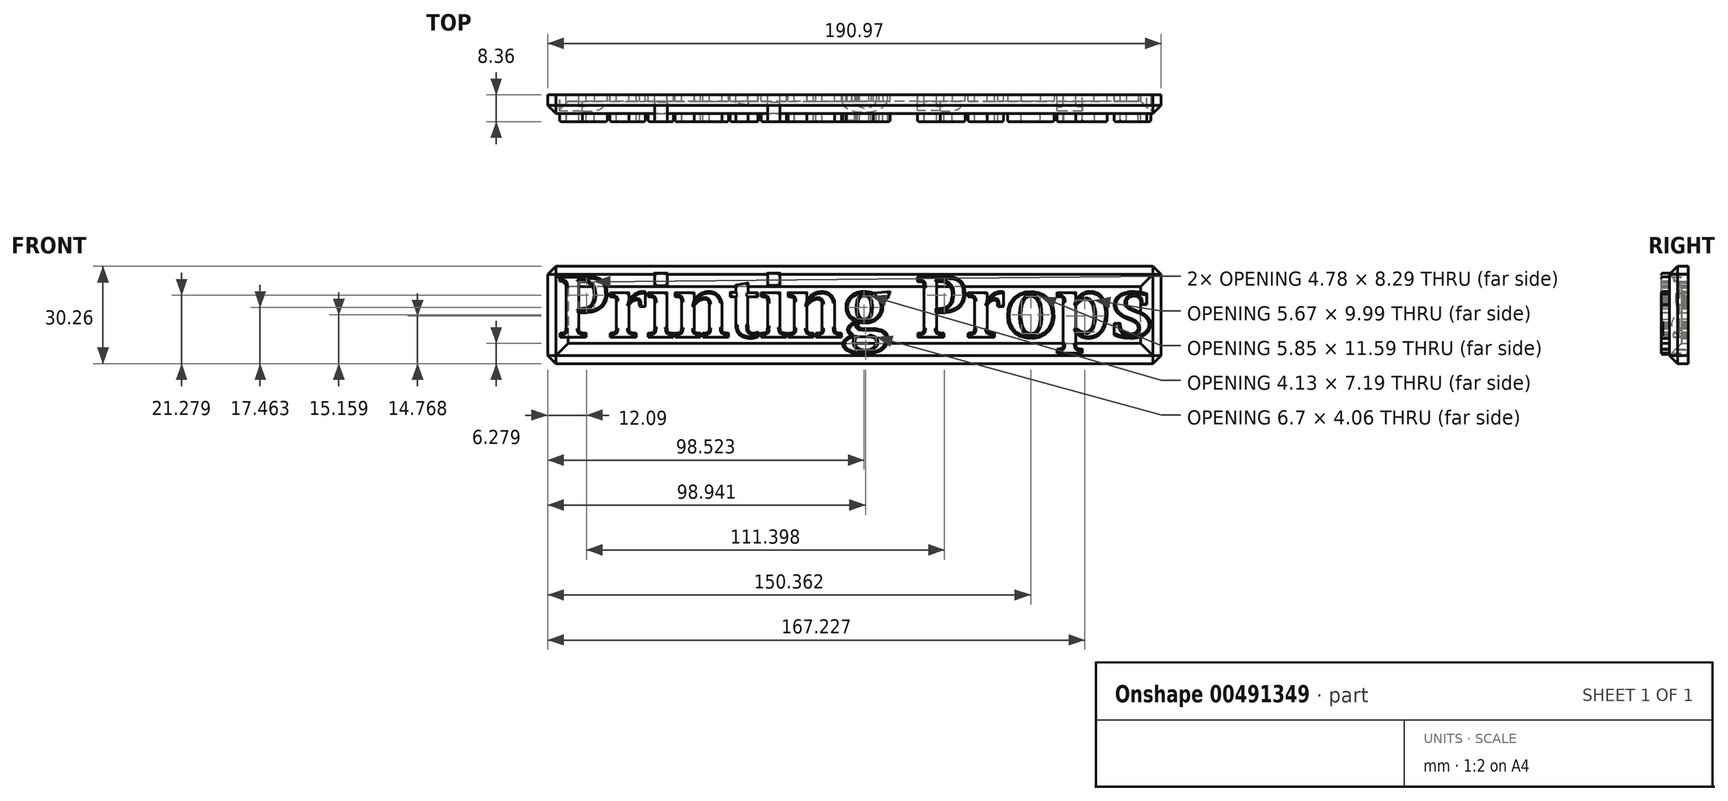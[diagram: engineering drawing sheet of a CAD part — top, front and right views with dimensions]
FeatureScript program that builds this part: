
annotation { "Feature Type Name" : "Feature", "Feature Type Description" : "" }
export const myFeature = defineFeature(function(context is Context, id is Id, definition is map)
    precondition{}
    {
        {
            var Q0;
            Q0=qCreatedBy(makeId("Front.planeOp"),FACE);
            var sketch = newSketch(context, id + "F0", { "sketchPlane" : qUnion([Q0])});
            skFitSpline(sketch, "E0", {"points": [v(-91.94, 12.22) * mm, v(-90.8, 12.2) * mm, v(-90.49, 12.06) * mm, v(-90.18, 11.82) * mm, v(-89.99, 10.88) * mm, v(-89.99, 10.32) * mm], "startDerivative": vector(4.95, 0.12) * mm, "endDerivative": vector(-0.1, -2.65) * mm});
            skFitSpline(sketch, "E1", {"points": [v(-91.84, -3.83) * mm, v(-90.83, -3.75) * mm, v(-90.33, -3.57) * mm, v(-90.09, -3.28) * mm, v(-89.99, -2.24) * mm], "startDerivative": vector(3.66, 0.14) * mm, "endDerivative": vector(0.08, 3.99) * mm});
            skFitSpline(sketch, "E2", {"points": [v(-85.99, -2.4) * mm, v(-85.92, -3.1) * mm, v(-85.68, -3.5) * mm, v(-85.3, -3.66) * mm, v(-84.73, -3.78) * mm, v(-83.76, -3.84) * mm], "startDerivative": vector(0.24, -3.52) * mm, "endDerivative": vector(4.1, -0.16) * mm});
            skFitSpline(sketch, "E3", {"points": [v(-85.98, 3.82) * mm, v(-84.6, 3.86) * mm, v(-83.12, 4.26) * mm, v(-82, 5.23) * mm, v(-81.55, 6.04) * mm, v(-81.33, 6.77) * mm, v(-81.2, 7.96) * mm, v(-81.24, 9.19) * mm, v(-81.58, 10.46) * mm, v(-82.35, 11.4) * mm, v(-83.21, 11.9) * mm, v(-83.91, 12.1) * mm, v(-85.98, 12.12) * mm], "startDerivative": vector(15.1, -0.2) * mm, "endDerivative": vector(-22.29, -0.17) * mm});
            skLineSegment(sketch, "E4", {"start": v(-85.98, 3.82) * mm, "end": v(-85.98, 12.12) * mm});
            skLineSegment(sketch, "E5", {"start": v(-89.99, 10.32) * mm, "end": v(-89.99, -2.24) * mm});
            skLineSegment(sketch, "E6", {"start": v(-85.99, -2.4) * mm, "end": v(-85.99, 2.51) * mm});
            skLineSegment(sketch, "E7", {"start": v(-91.94, 12.22) * mm, "end": v(-91.94, 13.6) * mm});
            skLineSegment(sketch, "E8", {"start": v(-91.94, 13.6) * mm, "end": v(-84.84, 13.6) * mm});
            skLineSegment(sketch, "E9", {"start": v(-91.84, -3.83) * mm, "end": v(-91.84, -5.1) * mm});
            skLineSegment(sketch, "E10", {"start": v(-91.84, -5.1) * mm, "end": v(-83.75, -5.1) * mm});
            skLineSegment(sketch, "E11", {"start": v(-83.75, -5.1) * mm, "end": v(-83.76, -3.84) * mm});
            skFitSpline(sketch, "E12", {"points": [v(-85.99, 2.51) * mm, v(-84.25, 2.51) * mm, v(-82.64, 2.64) * mm, v(-81.06, 2.99) * mm, v(-79.6, 3.66) * mm, v(-78.84, 4.24) * mm, v(-78.27, 4.85) * mm, v(-77.7, 5.78) * mm, v(-77.36, 6.72) * mm, v(-77.18, 7.66) * mm, v(-77.17, 8.86) * mm, v(-77.28, 10.04) * mm, v(-77.43, 10.75) * mm, v(-77.95, 11.78) * mm, v(-79.12, 12.92) * mm, v(-80.63, 13.48) * mm, v(-82.62, 13.65) * mm, v(-84.84, 13.6) * mm], "startDerivative": vector(26.06, -0.41) * mm, "endDerivative": vector(-29.4, -1.03) * mm});
            skLineSegment(sketch, "E13", {"start": v(-76.28, 7.51) * mm, "end": v(-76.28, 8.8) * mm});
            skLineSegment(sketch, "E14", {"start": v(-76.28, 8.8) * mm, "end": v(-70.38, 8.8) * mm});
            skLineSegment(sketch, "E15", {"start": v(-70.38, 8.8) * mm, "end": v(-70.38, 6.34) * mm});
            skLineSegment(sketch, "E16", {"start": v(-67.05, 4.44) * mm, "end": v(-65.31, 4.44) * mm});
            skLineSegment(sketch, "E17", {"start": v(-65.31, 4.44) * mm, "end": v(-65.31, 9.03) * mm});
            skLineSegment(sketch, "E18", {"start": v(-74.3, -2.36) * mm, "end": v(-74.3, 6.22) * mm});
            skLineSegment(sketch, "E19", {"start": v(-70.4, 4.83) * mm, "end": v(-70.4, -2.36) * mm});
            skLineSegment(sketch, "E20", {"start": v(-76.24, -3.81) * mm, "end": v(-76.24, -5.12) * mm});
            skLineSegment(sketch, "E21", {"start": v(-76.24, -5.12) * mm, "end": v(-68.07, -5.12) * mm});
            skLineSegment(sketch, "E22", {"start": v(-68.07, -5.12) * mm, "end": v(-68.07, -3.81) * mm});
            skFitSpline(sketch, "E23", {"points": [v(-76.28, 7.51) * mm, v(-75.6, 7.46) * mm, v(-75.08, 7.36) * mm, v(-74.68, 7.2) * mm, v(-74.47, 7) * mm, v(-74.35, 6.6) * mm, v(-74.3, 6.22) * mm], "startDerivative": vector(3.37, -0.21) * mm, "endDerivative": vector(0.24, -2.36) * mm});
            skFitSpline(sketch, "E24", {"points": [v(-70.38, 6.34) * mm, v(-69.87, 7.08) * mm, v(-69.4, 7.6) * mm, v(-68.86, 8.07) * mm, v(-68.26, 8.49) * mm, v(-67.53, 8.82) * mm, v(-66.76, 9.03) * mm, v(-65.99, 9.09) * mm, v(-65.31, 9.03) * mm], "startDerivative": vector(3.79, 5.74) * mm, "endDerivative": vector(5.61, -0.62) * mm});
            skFitSpline(sketch, "E25", {"points": [v(-70.4, 4.83) * mm, v(-70.07, 5.24) * mm, v(-69.6, 5.77) * mm, v(-69.03, 6.16) * mm, v(-68.41, 6.4) * mm, v(-67.8, 6.46) * mm, v(-67.47, 6.4) * mm, v(-67.3, 6.17) * mm, v(-67.05, 4.44) * mm], "startDerivative": vector(2.76, 3.54) * mm, "endDerivative": vector(1, -10.28) * mm});
            skFitSpline(sketch, "E26", {"points": [v(-76.24, -3.81) * mm, v(-75.25, -3.73) * mm, v(-74.8, -3.6) * mm, v(-74.51, -3.42) * mm, v(-74.37, -3.01) * mm, v(-74.3, -2.36) * mm], "startDerivative": vector(4.1, 0.22) * mm, "endDerivative": vector(0.3, 3.1) * mm});
            skFitSpline(sketch, "E27", {"points": [v(-70.4, -2.36) * mm, v(-70.27, -3.13) * mm, v(-70.04, -3.49) * mm, v(-69.6, -3.65) * mm, v(-68.92, -3.78) * mm, v(-68.07, -3.81) * mm], "startDerivative": vector(0.38, -3.73) * mm, "endDerivative": vector(3.76, -0.02) * mm});
            skLineSegment(sketch, "E28.bottom", {"start": v(-62.4, 14.84) * mm, "end": v(-58.48, 14.84) * mm});
            skLineSegment(sketch, "E28.top", {"start": v(-62.4, 10.95) * mm, "end": v(-58.48, 10.95) * mm});
            skLineSegment(sketch, "E28.left", {"start": v(-62.4, 14.84) * mm, "end": v(-62.4, 10.95) * mm});
            skLineSegment(sketch, "E28.right", {"start": v(-58.48, 14.84) * mm, "end": v(-58.48, 10.95) * mm});
            skLineSegment(sketch, "E29", {"start": v(-64.35, 7.53) * mm, "end": v(-64.35, 8.77) * mm});
            skLineSegment(sketch, "E30", {"start": v(-64.35, 8.77) * mm, "end": v(-58.52, 8.77) * mm});
            skLineSegment(sketch, "E31", {"start": v(-58.52, 8.77) * mm, "end": v(-58.52, -2.05) * mm});
            skLineSegment(sketch, "E32", {"start": v(-56.5, -3.83) * mm, "end": v(-56.5, -5.1) * mm});
            skLineSegment(sketch, "E33", {"start": v(-56.5, -5.1) * mm, "end": v(-64.37, -5.1) * mm});
            skLineSegment(sketch, "E34", {"start": v(-64.37, -5.1) * mm, "end": v(-64.37, -3.83) * mm});
            skLineSegment(sketch, "E35", {"start": v(-62.38, 5.71) * mm, "end": v(-62.38, -1.9) * mm});
            skFitSpline(sketch, "E36", {"points": [v(-64.35, 7.53) * mm, v(-63.53, 7.44) * mm, v(-62.95, 7.29) * mm, v(-62.64, 7.06) * mm, v(-62.47, 6.74) * mm, v(-62.4, 6.24) * mm, v(-62.38, 5.71) * mm], "startDerivative": vector(4.02, -0.33) * mm, "endDerivative": vector(0.08, -3.14) * mm});
            skFitSpline(sketch, "E37", {"points": [v(-64.37, -3.83) * mm, v(-63.3, -3.75) * mm, v(-62.9, -3.62) * mm, v(-62.65, -3.46) * mm, v(-62.5, -3.1) * mm, v(-62.38, -1.9) * mm], "startDerivative": vector(4.6, 0.22) * mm, "endDerivative": vector(0.28, 4.9) * mm});
            skFitSpline(sketch, "E38", {"points": [v(-58.52, -2.05) * mm, v(-58.43, -3.02) * mm, v(-58.18, -3.57) * mm, v(-56.5, -3.83) * mm], "startDerivative": vector(0.24, -3.2) * mm, "endDerivative": vector(4.85, -0.19) * mm});
            skLineSegment(sketch, "E39", {"start": v(-56, 7.49) * mm, "end": v(-56, 8.79) * mm});
            skLineSegment(sketch, "E40", {"start": v(-56, 8.79) * mm, "end": v(-50.1, 8.79) * mm});
            skLineSegment(sketch, "E41", {"start": v(-50.1, 8.79) * mm, "end": v(-50.1, 6.41) * mm});
            skLineSegment(sketch, "E42", {"start": v(-54.03, 5.98) * mm, "end": v(-54.03, -2.23) * mm});
            skLineSegment(sketch, "E43", {"start": v(-55.98, -3.83) * mm, "end": v(-55.98, -5.1) * mm});
            skLineSegment(sketch, "E44", {"start": v(-55.98, -5.1) * mm, "end": v(-48.15, -5.1) * mm});
            skLineSegment(sketch, "E45", {"start": v(-48.15, -5.1) * mm, "end": v(-48.15, -3.83) * mm});
            skLineSegment(sketch, "E46", {"start": v(-50.08, -2.32) * mm, "end": v(-50.08, 4.7) * mm});
            skLineSegment(sketch, "E47", {"start": v(-45.4, 5.16) * mm, "end": v(-45.4, -2.35) * mm});
            skLineSegment(sketch, "E48", {"start": v(-47.32, -3.83) * mm, "end": v(-47.32, -5.1) * mm});
            skLineSegment(sketch, "E49", {"start": v(-47.32, -5.1) * mm, "end": v(-39.39, -5.1) * mm});
            skLineSegment(sketch, "E50", {"start": v(-39.39, -5.1) * mm, "end": v(-39.39, -3.83) * mm});
            skLineSegment(sketch, "E51", {"start": v(-41.45, -2.07) * mm, "end": v(-41.45, 5.52) * mm});
            skFitSpline(sketch, "E52", {"points": [v(-56, 7.49) * mm, v(-54.99, 7.4) * mm, v(-54.35, 7.2) * mm, v(-54.03, 5.98) * mm], "startDerivative": vector(3.08, -0.26) * mm, "endDerivative": vector(-0.08, -4.62) * mm});
            skFitSpline(sketch, "E53", {"points": [v(-55.98, -3.83) * mm, v(-55.01, -3.78) * mm, v(-54.43, -3.6) * mm, v(-54.15, -3.23) * mm, v(-54.03, -2.23) * mm], "startDerivative": vector(3.56, 0.06) * mm, "endDerivative": vector(0.2, 3.88) * mm});
            skFitSpline(sketch, "E54", {"points": [v(-50.08, -2.32) * mm, v(-49.98, -3.27) * mm, v(-49.48, -3.7) * mm, v(-48.15, -3.83) * mm], "startDerivative": vector(-0.03, -3.17) * mm, "endDerivative": vector(3.77, -0.05) * mm});
            skFitSpline(sketch, "E55", {"points": [v(-47.32, -3.83) * mm, v(-46.35, -3.77) * mm, v(-45.8, -3.63) * mm, v(-45.51, -3.33) * mm, v(-45.4, -2.35) * mm], "startDerivative": vector(3.53, 0.14) * mm, "endDerivative": vector(0.06, 3.83) * mm});
            skFitSpline(sketch, "E56", {"points": [v(-41.45, -2.07) * mm, v(-41.36, -3.08) * mm, v(-41.14, -3.5) * mm, v(-40.34, -3.77) * mm, v(-39.39, -3.83) * mm], "startDerivative": vector(0.19, -4) * mm, "endDerivative": vector(3.45, -0.05) * mm});
            skFitSpline(sketch, "E57", {"points": [v(-50.08, 4.7) * mm, v(-49.53, 5.34) * mm, v(-48.68, 6.07) * mm, v(-47.82, 6.52) * mm, v(-47.1, 6.66) * mm, v(-46.39, 6.65) * mm, v(-45.93, 6.46) * mm, v(-45.54, 5.9) * mm, v(-45.4, 5.16) * mm], "startDerivative": vector(3.9, 4.85) * mm, "endDerivative": vector(0.58, -6.2) * mm});
            skFitSpline(sketch, "E58", {"points": [v(-50.1, 6.41) * mm, v(-49.57, 7.18) * mm, v(-48.51, 8.17) * mm, v(-47.15, 8.84) * mm, v(-45.81, 9.07) * mm, v(-44.56, 9.03) * mm, v(-43.72, 8.77) * mm, v(-42.97, 8.32) * mm, v(-42.37, 7.74) * mm, v(-41.9, 7) * mm, v(-41.45, 5.52) * mm], "startDerivative": vector(5.14, 8.27) * mm, "endDerivative": vector(1, -14.05) * mm});
            skLineSegment(sketch, "E59", {"start": v(-38.9, 7.42) * mm, "end": v(-38.9, 8.81) * mm});
            skLineSegment(sketch, "E60", {"start": v(-38.9, 8.81) * mm, "end": v(-37.15, 8.81) * mm});
            skLineSegment(sketch, "E61", {"start": v(-37.15, 8.81) * mm, "end": v(-37.15, 11.09) * mm});
            skLineSegment(sketch, "E62", {"start": v(-37.15, 11.09) * mm, "end": v(-33.32, 11.8) * mm});
            skLineSegment(sketch, "E63", {"start": v(-33.32, 11.8) * mm, "end": v(-33.32, 8.76) * mm});
            skLineSegment(sketch, "E64", {"start": v(-33.32, 8.76) * mm, "end": v(-30.25, 8.76) * mm});
            skLineSegment(sketch, "E65", {"start": v(-30.25, 8.76) * mm, "end": v(-30.25, 7.43) * mm});
            skLineSegment(sketch, "E66", {"start": v(-30.25, 7.43) * mm, "end": v(-33.36, 7.43) * mm});
            skLineSegment(sketch, "E67", {"start": v(-33.36, 7.43) * mm, "end": v(-33.36, -1.22) * mm});
            skLineSegment(sketch, "E68", {"start": v(-38.9, 7.42) * mm, "end": v(-37.15, 7.42) * mm});
            skLineSegment(sketch, "E69", {"start": v(-37.15, 7.42) * mm, "end": v(-37.15, -1.26) * mm});
            skLineSegment(sketch, "E70", {"start": v(-30.12, -3.52) * mm, "end": v(-30.12, -5.02) * mm});
            skFitSpline(sketch, "E71", {"points": [v(-37.15, -1.26) * mm, v(-37.07, -2.2) * mm, v(-36.66, -3.4) * mm, v(-35.91, -4.41) * mm, v(-34.77, -5.1) * mm, v(-33.27, -5.41) * mm, v(-32.17, -5.46) * mm, v(-30.12, -5.02) * mm], "startDerivative": vector(0.18, -7.56) * mm, "endDerivative": vector(12.49, 3.28) * mm});
            skFitSpline(sketch, "E72", {"points": [v(-33.36, -1.22) * mm, v(-33.26, -2.35) * mm, v(-32.94, -3.35) * mm, v(-32.32, -3.75) * mm, v(-31.4, -3.83) * mm, v(-30.12, -3.52) * mm], "startDerivative": vector(0.26, -8.8) * mm, "endDerivative": vector(5.84, 1.77) * mm});
            skLineSegment(sketch, "E73.bottom", {"start": v(-27.2, 11.02) * mm, "end": v(-23.34, 11.02) * mm});
            skLineSegment(sketch, "E73.top", {"start": v(-27.2, 14.83) * mm, "end": v(-23.34, 14.83) * mm});
            skLineSegment(sketch, "E73.left", {"start": v(-27.2, 11.02) * mm, "end": v(-27.2, 14.83) * mm});
            skLineSegment(sketch, "E73.right", {"start": v(-23.34, 11.02) * mm, "end": v(-23.34, 14.83) * mm});
            skLineSegment(sketch, "E74", {"start": v(-29.18, 7.43) * mm, "end": v(-29.18, 8.76) * mm});
            skLineSegment(sketch, "E75", {"start": v(-29.18, 8.76) * mm, "end": v(-23.36, 8.76) * mm});
            skLineSegment(sketch, "E76", {"start": v(-23.36, 8.76) * mm, "end": v(-23.36, -2.06) * mm});
            skLineSegment(sketch, "E77", {"start": v(-27.23, 5.37) * mm, "end": v(-27.23, -1.69) * mm});
            skLineSegment(sketch, "E78", {"start": v(-29.22, -3.84) * mm, "end": v(-29.22, -5.11) * mm});
            skLineSegment(sketch, "E79", {"start": v(-29.22, -5.11) * mm, "end": v(-21.32, -5.11) * mm});
            skLineSegment(sketch, "E80", {"start": v(-21.32, -5.11) * mm, "end": v(-21.32, -3.82) * mm});
            skFitSpline(sketch, "E81", {"points": [v(-29.22, -3.84) * mm, v(-28.3, -3.77) * mm, v(-27.73, -3.63) * mm, v(-27.38, -3.35) * mm, v(-27.29, -2.9) * mm, v(-27.23, -1.69) * mm], "startDerivative": vector(4.22, 0.2) * mm, "endDerivative": vector(0.23, 5.1) * mm});
            skFitSpline(sketch, "E82", {"points": [v(-23.36, -2.06) * mm, v(-23.21, -3.14) * mm, v(-22.92, -3.56) * mm, v(-22.3, -3.75) * mm, v(-21.32, -3.82) * mm], "startDerivative": vector(0.28, -4.1) * mm, "endDerivative": vector(3.66, -0.12) * mm});
            skFitSpline(sketch, "E83", {"points": [v(-29.18, 7.43) * mm, v(-28.25, 7.38) * mm, v(-27.79, 7.29) * mm, v(-27.51, 7.12) * mm, v(-27.3, 6.65) * mm, v(-27.23, 5.37) * mm], "startDerivative": vector(4.22, -0.13) * mm, "endDerivative": vector(0.01, -5.13) * mm});
            skLineSegment(sketch, "E84", {"start": v(-20.86, 7.48) * mm, "end": v(-20.86, 8.77) * mm});
            skLineSegment(sketch, "E85", {"start": v(-20.86, 8.77) * mm, "end": v(-14.95, 8.77) * mm});
            skLineSegment(sketch, "E86", {"start": v(-14.95, 8.77) * mm, "end": v(-14.95, 6.4) * mm});
            skLineSegment(sketch, "E87", {"start": v(-18.88, 5.97) * mm, "end": v(-18.88, -2.24) * mm});
            skLineSegment(sketch, "E88", {"start": v(-20.84, -3.85) * mm, "end": v(-20.84, -5.12) * mm});
            skLineSegment(sketch, "E89", {"start": v(-20.84, -5.12) * mm, "end": v(-13.01, -5.12) * mm});
            skLineSegment(sketch, "E90", {"start": v(-13.01, -5.12) * mm, "end": v(-13.01, -3.85) * mm});
            skLineSegment(sketch, "E91", {"start": v(-14.94, -2.33) * mm, "end": v(-14.94, 4.7) * mm});
            skLineSegment(sketch, "E92", {"start": v(-10.26, 5.14) * mm, "end": v(-10.26, -2.36) * mm});
            skLineSegment(sketch, "E93", {"start": v(-12.17, -3.85) * mm, "end": v(-12.17, -5.12) * mm});
            skLineSegment(sketch, "E94", {"start": v(-12.17, -5.12) * mm, "end": v(-4.24, -5.12) * mm});
            skLineSegment(sketch, "E95", {"start": v(-4.24, -5.12) * mm, "end": v(-4.24, -3.85) * mm});
            skLineSegment(sketch, "E96", {"start": v(-6.3, -2.08) * mm, "end": v(-6.3, 5.51) * mm});
            skFitSpline(sketch, "E97", {"points": [v(-20.86, 7.48) * mm, v(-19.84, 7.39) * mm, v(-19.2, 7.19) * mm, v(-18.88, 5.97) * mm], "startDerivative": vector(3.08, -0.26) * mm, "endDerivative": vector(-0.08, -4.62) * mm});
            skFitSpline(sketch, "E98", {"points": [v(-20.84, -3.85) * mm, v(-19.87, -3.8) * mm, v(-19.3, -3.6) * mm, v(-19.01, -3.25) * mm, v(-18.88, -2.24) * mm], "startDerivative": vector(3.56, 0.06) * mm, "endDerivative": vector(0.2, 3.88) * mm});
            skFitSpline(sketch, "E99", {"points": [v(-14.94, -2.33) * mm, v(-14.84, -3.29) * mm, v(-14.34, -3.71) * mm, v(-13.01, -3.85) * mm], "startDerivative": vector(-0.03, -3.17) * mm, "endDerivative": vector(3.77, -0.05) * mm});
            skFitSpline(sketch, "E100", {"points": [v(-12.17, -3.85) * mm, v(-11.2, -3.78) * mm, v(-10.66, -3.64) * mm, v(-10.37, -3.34) * mm, v(-10.26, -2.36) * mm], "startDerivative": vector(3.53, 0.14) * mm, "endDerivative": vector(0.06, 3.83) * mm});
            skFitSpline(sketch, "E101", {"points": [v(-6.3, -2.08) * mm, v(-6.22, -3.1) * mm, v(-6, -3.5) * mm, v(-5.2, -3.78) * mm, v(-4.24, -3.85) * mm], "startDerivative": vector(0.19, -4) * mm, "endDerivative": vector(3.45, -0.05) * mm});
            skFitSpline(sketch, "E102", {"points": [v(-14.94, 4.7) * mm, v(-14.4, 5.33) * mm, v(-13.54, 6.06) * mm, v(-12.68, 6.5) * mm, v(-11.97, 6.65) * mm, v(-11.25, 6.64) * mm, v(-10.8, 6.45) * mm, v(-10.4, 5.89) * mm, v(-10.26, 5.14) * mm], "startDerivative": vector(3.9, 4.85) * mm, "endDerivative": vector(0.58, -6.2) * mm});
            skFitSpline(sketch, "E103", {"points": [v(-14.95, 6.4) * mm, v(-14.42, 7.17) * mm, v(-13.37, 8.16) * mm, v(-12, 8.82) * mm, v(-10.67, 9.06) * mm, v(-9.41, 9.01) * mm, v(-8.58, 8.76) * mm, v(-7.82, 8.3) * mm, v(-7.23, 7.73) * mm, v(-6.77, 7) * mm, v(-6.3, 5.51) * mm], "startDerivative": vector(5.14, 8.27) * mm, "endDerivative": vector(1, -14.05) * mm});
            skFitSpline(sketch, "E104", {"points": [v(19.46, 12.2) * mm, v(20.59, 12.17) * mm, v(20.91, 12.04) * mm, v(21.22, 11.8) * mm, v(21.41, 10.86) * mm, v(21.41, 10.3) * mm], "startDerivative": vector(4.95, 0.12) * mm, "endDerivative": vector(-0.1, -2.65) * mm});
            skFitSpline(sketch, "E105", {"points": [v(19.56, -3.85) * mm, v(20.57, -3.77) * mm, v(21.07, -3.59) * mm, v(21.31, -3.3) * mm, v(21.41, -2.26) * mm], "startDerivative": vector(3.66, 0.14) * mm, "endDerivative": vector(0.08, 3.99) * mm});
            skFitSpline(sketch, "E106", {"points": [v(25.41, -2.43) * mm, v(25.48, -3.12) * mm, v(25.72, -3.51) * mm, v(26.1, -3.68) * mm, v(26.67, -3.8) * mm, v(27.64, -3.86) * mm], "startDerivative": vector(0.24, -3.52) * mm, "endDerivative": vector(4.1, -0.16) * mm});
            skFitSpline(sketch, "E107", {"points": [v(25.42, 3.8) * mm, v(26.8, 3.84) * mm, v(28.28, 4.24) * mm, v(29.4, 5.2) * mm, v(29.85, 6.02) * mm, v(30.07, 6.75) * mm, v(30.2, 7.94) * mm, v(30.16, 9.17) * mm, v(29.82, 10.44) * mm, v(29.05, 11.37) * mm, v(28.18, 11.89) * mm, v(27.48, 12.09) * mm, v(25.42, 12.1) * mm], "startDerivative": vector(15.1, -0.2) * mm, "endDerivative": vector(-22.29, -0.17) * mm});
            skLineSegment(sketch, "E108", {"start": v(25.42, 3.8) * mm, "end": v(25.42, 12.1) * mm});
            skLineSegment(sketch, "E109", {"start": v(21.41, 10.3) * mm, "end": v(21.41, -2.26) * mm});
            skLineSegment(sketch, "E110", {"start": v(25.41, -2.43) * mm, "end": v(25.41, 2.5) * mm});
            skLineSegment(sketch, "E111", {"start": v(19.46, 12.2) * mm, "end": v(19.46, 13.6) * mm});
            skLineSegment(sketch, "E112", {"start": v(19.46, 13.6) * mm, "end": v(26.56, 13.6) * mm});
            skLineSegment(sketch, "E113", {"start": v(19.56, -3.85) * mm, "end": v(19.56, -5.13) * mm});
            skLineSegment(sketch, "E114", {"start": v(19.56, -5.13) * mm, "end": v(27.65, -5.13) * mm});
            skLineSegment(sketch, "E115", {"start": v(27.65, -5.13) * mm, "end": v(27.64, -3.86) * mm});
            skFitSpline(sketch, "E116", {"points": [v(25.41, 2.5) * mm, v(27.15, 2.5) * mm, v(28.76, 2.62) * mm, v(30.33, 2.97) * mm, v(31.8, 3.64) * mm, v(32.56, 4.22) * mm, v(33.13, 4.83) * mm, v(33.7, 5.76) * mm, v(34.03, 6.7) * mm, v(34.22, 7.64) * mm, v(34.23, 8.84) * mm, v(34.11, 10.02) * mm, v(33.97, 10.73) * mm, v(33.45, 11.76) * mm, v(32.28, 12.9) * mm, v(30.77, 13.46) * mm, v(28.78, 13.63) * mm, v(26.56, 13.6) * mm], "startDerivative": vector(26.06, -0.41) * mm, "endDerivative": vector(-29.4, -1.03) * mm});
            skLineSegment(sketch, "E117", {"start": v(35.2, 7.5) * mm, "end": v(35.2, 8.79) * mm});
            skLineSegment(sketch, "E118", {"start": v(35.2, 8.79) * mm, "end": v(41.09, 8.79) * mm});
            skLineSegment(sketch, "E119", {"start": v(41.09, 8.79) * mm, "end": v(41.09, 6.33) * mm});
            skLineSegment(sketch, "E120", {"start": v(44.42, 4.44) * mm, "end": v(46.16, 4.44) * mm});
            skLineSegment(sketch, "E121", {"start": v(46.16, 4.44) * mm, "end": v(46.16, 9.03) * mm});
            skLineSegment(sketch, "E122", {"start": v(37.17, -2.37) * mm, "end": v(37.17, 6.22) * mm});
            skLineSegment(sketch, "E123", {"start": v(41.08, 4.83) * mm, "end": v(41.08, -2.37) * mm});
            skLineSegment(sketch, "E124", {"start": v(35.23, -3.82) * mm, "end": v(35.23, -5.12) * mm});
            skLineSegment(sketch, "E125", {"start": v(35.23, -5.12) * mm, "end": v(43.4, -5.12) * mm});
            skLineSegment(sketch, "E126", {"start": v(43.4, -5.12) * mm, "end": v(43.4, -3.82) * mm});
            skFitSpline(sketch, "E127", {"points": [v(35.2, 7.5) * mm, v(35.86, 7.46) * mm, v(36.39, 7.36) * mm, v(36.79, 7.2) * mm, v(37, 7) * mm, v(37.13, 6.6) * mm, v(37.17, 6.22) * mm], "startDerivative": vector(3.37, -0.21) * mm, "endDerivative": vector(0.24, -2.36) * mm});
            skFitSpline(sketch, "E128", {"points": [v(41.09, 6.33) * mm, v(41.6, 7.08) * mm, v(42.06, 7.6) * mm, v(42.61, 8.07) * mm, v(43.21, 8.48) * mm, v(43.94, 8.82) * mm, v(44.71, 9.03) * mm, v(45.48, 9.08) * mm, v(46.16, 9.03) * mm], "startDerivative": vector(3.79, 5.74) * mm, "endDerivative": vector(5.61, -0.62) * mm});
            skFitSpline(sketch, "E129", {"points": [v(41.08, 4.83) * mm, v(41.4, 5.24) * mm, v(41.87, 5.77) * mm, v(42.45, 6.16) * mm, v(43.06, 6.4) * mm, v(43.67, 6.46) * mm, v(44, 6.4) * mm, v(44.18, 6.17) * mm, v(44.42, 4.44) * mm], "startDerivative": vector(2.76, 3.54) * mm, "endDerivative": vector(1, -10.28) * mm});
            skFitSpline(sketch, "E130", {"points": [v(35.23, -3.82) * mm, v(36.23, -3.73) * mm, v(36.66, -3.61) * mm, v(36.96, -3.43) * mm, v(37.1, -3.02) * mm, v(37.17, -2.37) * mm], "startDerivative": vector(4.1, 0.22) * mm, "endDerivative": vector(0.3, 3.1) * mm});
            skFitSpline(sketch, "E131", {"points": [v(41.08, -2.37) * mm, v(41.2, -3.13) * mm, v(41.43, -3.5) * mm, v(41.87, -3.65) * mm, v(42.55, -3.78) * mm, v(43.4, -3.82) * mm], "startDerivative": vector(0.38, -3.73) * mm, "endDerivative": vector(3.76, -0.02) * mm});
            skLineSegment(sketch, "E132", {"start": v(5.69, 8.61) * mm, "end": v(10.93, 9.05) * mm});
            skLineSegment(sketch, "E133", {"start": v(10.93, 9.05) * mm, "end": v(10.12, 6.9) * mm});
            skLineSegment(sketch, "E134", {"start": v(10.12, 6.9) * mm, "end": v(7.42, 7.3) * mm});
            skLineSegment(sketch, "E135", {"start": v(0.4, -5) * mm, "end": v(4.26, -5) * mm});
            skFitSpline(sketch, "E136", {"points": [v(5.69, 8.61) * mm, v(4.94, 8.9) * mm, v(3.5, 9.08) * mm, v(1.93, 9.07) * mm, v(0.1, 8.61) * mm, v(-1.48, 7.52) * mm, v(-2.22, 6.61) * mm, v(-2.7, 5.37) * mm, v(-2.82, 3.7) * mm, v(-2.56, 2.47) * mm, v(-2.16, 1.62) * mm, v(-1.28, 0.67) * mm, v(0.22, -0.18) * mm], "startDerivative": vector(-10.73, 5.02) * mm, "endDerivative": vector(17.3, -8.4) * mm});
            skFitSpline(sketch, "E137", {"points": [v(0.22, -0.18) * mm, v(-0.47, -0.51) * mm, v(-1.22, -1.03) * mm, v(-1.85, -1.6) * mm, v(-2.22, -2.2) * mm, v(-2.38, -2.82) * mm, v(-2.13, -3.55) * mm, v(-1.63, -4.15) * mm, v(-1.08, -4.56) * mm, v(-1.08, -4.57) * mm], "startDerivative": vector(-5.47, -2.43) * mm, "endDerivative": vector(-0.21, -0.37) * mm});
            skFitSpline(sketch, "E138", {"points": [v(-1.08, -4.57) * mm, v(-1.9, -4.94) * mm, v(-2.69, -5.4) * mm, v(-3.26, -5.92) * mm, v(-3.7, -6.66) * mm, v(-3.81, -7.51) * mm, v(-3.42, -8.56) * mm, v(-2.02, -9.53) * mm, v(0.33, -10.27) * mm, v(3.33, -10.44) * mm, v(5.6, -10.18) * mm, v(7.5, -9.53) * mm, v(8.67, -8.8) * mm, v(9.43, -8.03) * mm, v(9.92, -7.09) * mm, v(10.13, -5.8) * mm, v(9.88, -4.2) * mm, v(8.89, -3.15) * mm, v(7.26, -2.64) * mm, v(5.8, -2.46) * mm, v(2.14, -2.45) * mm, v(1.32, -2.31) * mm, v(0.85, -2.05) * mm, v(0.65, -1.76) * mm, v(0.75, -1.25) * mm, v(1.44, -0.47) * mm], "startDerivative": vector(-24.73, -10.67) * mm, "endDerivative": vector(23.18, 21.72) * mm});
            skFitSpline(sketch, "E139", {"points": [v(0.4, -5) * mm, v(0.06, -5.87) * mm, v(-0.1, -6.68) * mm, v(0.22, -7.74) * mm, v(1.12, -8.58) * mm, v(2.27, -9.04) * mm, v(3.54, -9.1) * mm, v(4.78, -8.85) * mm, v(5.75, -8.24) * mm, v(6.32, -7.54) * mm, v(6.57, -6.92) * mm, v(6.6, -6.14) * mm, v(6.13, -5.49) * mm, v(5.32, -5.1) * mm, v(4.26, -5) * mm], "startDerivative": vector(-5.28, -12.73) * mm, "endDerivative": vector(-14.88, 0.2) * mm});
            skFitSpline(sketch, "E140", {"points": [v(7.42, 7.3) * mm, v(7.83, 6.82) * mm, v(8.23, 6.07) * mm, v(8.5, 5.18) * mm, v(8.59, 4.25) * mm, v(8.5, 3.16) * mm, v(8.15, 2.2) * mm, v(7.5, 1.18) * mm, v(6.83, 0.5) * mm, v(5.9, -0.1) * mm, v(4.76, -0.54) * mm, v(3.6, -0.69) * mm, v(2.48, -0.65) * mm, v(1.44, -0.47) * mm], "startDerivative": vector(6.96, -7.28) * mm, "endDerivative": vector(-13.13, 2.78) * mm});
            skFitSpline(sketch, "E141", {"points": [v(2.85, 7.75) * mm, v(2.5, 7.74) * mm, v(1.68, 7.3) * mm, v(1.05, 6.18) * mm, v(0.82, 4.7) * mm, v(0.8, 3.13) * mm, v(1.21, 1.55) * mm, v(1.86, 0.8) * mm, v(2.44, 0.55) * mm, v(2.96, 0.5) * mm, v(3.6, 0.64) * mm, v(4.08, 0.97) * mm, v(4.44, 1.42) * mm, v(4.75, 2.2) * mm, v(4.9, 3.26) * mm, v(4.89, 4.94) * mm, v(4.74, 6.07) * mm, v(4.49, 6.72) * mm, v(4.06, 7.3) * mm, v(3.62, 7.62) * mm, v(2.85, 7.75) * mm]});
            skFitSpline(sketch, "E142", {"points": [v(55.13, 9.1) * mm, v(54.33, 9.09) * mm, v(53.1, 8.98) * mm, v(51.3, 8.42) * mm, v(50.21, 7.82) * mm, v(49.05, 6.72) * mm, v(48.07, 5.1) * mm, v(47.52, 2.74) * mm, v(47.57, 0) * mm, v(48.5, -2.4) * mm, v(49.74, -3.83) * mm, v(51.21, -4.76) * mm, v(53.17, -5.36) * mm, v(54.83, -5.44) * mm, v(55.87, -5.4) * mm, v(57.33, -5.12) * mm, v(58.67, -4.54) * mm, v(59.52, -3.94) * mm, v(60.35, -3.14) * mm, v(61.1, -2.04) * mm, v(61.6, -0.7) * mm, v(61.85, 0.48) * mm, v(61.94, 2.23) * mm, v(61.72, 3.94) * mm, v(61.12, 5.65) * mm, v(60.44, 6.63) * mm, v(59.18, 7.82) * mm, v(57.87, 8.54) * mm, v(56.36, 8.96) * mm, v(55.13, 9.1) * mm]});
            skFitSpline(sketch, "E143", {"points": [v(55.28, 7.64) * mm, v(54.8, 7.66) * mm, v(54.1, 7.57) * mm, v(53.38, 7.24) * mm, v(52.74, 6.62) * mm, v(52.22, 5.61) * mm, v(51.9, 4.2) * mm, v(51.75, 2.9) * mm, v(51.72, 1.12) * mm, v(51.84, -0.32) * mm, v(52.14, -1.79) * mm, v(52.5, -2.6) * mm, v(53, -3.3) * mm, v(53.98, -3.93) * mm, v(55.11, -3.98) * mm, v(55.54, -3.9) * mm, v(56.31, -3.4) * mm, v(56.92, -2.54) * mm, v(57.19, -1.82) * mm, v(57.48, -0.68) * mm, v(57.62, 1.07) * mm, v(57.61, 2.91) * mm, v(57.45, 4.56) * mm, v(57.11, 5.79) * mm, v(56.52, 6.78) * mm, v(55.97, 7.34) * mm, v(55.28, 7.64) * mm]});
            skLineSegment(sketch, "E144", {"start": v(62.88, 7.52) * mm, "end": v(62.88, 8.76) * mm});
            skLineSegment(sketch, "E145", {"start": v(62.88, 8.76) * mm, "end": v(68.71, 8.76) * mm});
            skLineSegment(sketch, "E146", {"start": v(68.71, 8.76) * mm, "end": v(68.71, 6.34) * mm});
            skLineSegment(sketch, "E147", {"start": v(64.82, 5.78) * mm, "end": v(64.82, -7.06) * mm});
            skLineSegment(sketch, "E148", {"start": v(62.86, -8.83) * mm, "end": v(62.86, -10.06) * mm});
            skLineSegment(sketch, "E149", {"start": v(62.86, -10.06) * mm, "end": v(70.75, -10.06) * mm});
            skLineSegment(sketch, "E150", {"start": v(70.75, -10.06) * mm, "end": v(70.75, -8.84) * mm});
            skLineSegment(sketch, "E151", {"start": v(68.71, -3.82) * mm, "end": v(68.71, -7.05) * mm});
            skLineSegment(sketch, "E152", {"start": v(68.71, -2.23) * mm, "end": v(68.71, 4.78) * mm});
            skFitSpline(sketch, "E153", {"points": [v(62.88, 7.52) * mm, v(63.89, 7.44) * mm, v(64.47, 7.24) * mm, v(64.78, 6.7) * mm, v(64.82, 5.78) * mm], "startDerivative": vector(3.75, -0.18) * mm, "endDerivative": vector(-0.12, -3.6) * mm});
            skFitSpline(sketch, "E154", {"points": [v(64.82, -7.06) * mm, v(64.76, -8.05) * mm, v(64.63, -8.41) * mm, v(64.1, -8.66) * mm, v(62.86, -8.83) * mm], "startDerivative": vector(-0.18, -3.86) * mm, "endDerivative": vector(-4.18, -0.42) * mm});
            skFitSpline(sketch, "E155", {"points": [v(68.71, -7.05) * mm, v(68.86, -8.09) * mm, v(69.13, -8.52) * mm, v(69.73, -8.71) * mm, v(70.75, -8.84) * mm], "startDerivative": vector(0.34, -3.94) * mm, "endDerivative": vector(3.75, -0.42) * mm});
            skFitSpline(sketch, "E156", {"points": [v(68.71, 4.78) * mm, v(69.45, 5.55) * mm, v(70.44, 6.27) * mm, v(71.44, 6.58) * mm, v(72.46, 6.48) * mm, v(73.35, 5.86) * mm, v(73.96, 4.78) * mm, v(74.33, 2.88) * mm, v(74.36, 0.9) * mm, v(74.17, -0.63) * mm, v(73.76, -1.98) * mm, v(73.04, -2.96) * mm, v(72.27, -3.41) * mm, v(71.43, -3.56) * mm, v(70.4, -3.33) * mm, v(68.71, -2.23) * mm], "startDerivative": vector(11.46, 12.73) * mm, "endDerivative": vector(-20.93, 15.63) * mm});
            skFitSpline(sketch, "E157", {"points": [v(68.71, -3.82) * mm, v(69.64, -4.55) * mm, v(70.62, -5.11) * mm, v(71.9, -5.43) * mm, v(73.26, -5.44) * mm, v(74.63, -5.12) * mm, v(75.49, -4.69) * mm, v(76.42, -3.91) * mm, v(77.32, -2.73) * mm, v(77.88, -1.44) * mm, v(78.28, 0) * mm, v(78.47, 2) * mm, v(78.28, 4.31) * mm, v(77.67, 6.22) * mm, v(76.59, 7.77) * mm, v(75.5, 8.6) * mm, v(74.03, 9.06) * mm, v(72.28, 9.05) * mm, v(71.12, 8.69) * mm, v(70, 7.95) * mm, v(68.71, 6.34) * mm], "startDerivative": vector(20.6, -17.26) * mm, "endDerivative": vector(-21.59, -30.35) * mm});
            skLineSegment(sketch, "E158", {"start": v(88.9, 5.04) * mm, "end": v(90.83, 5.04) * mm});
            skLineSegment(sketch, "E159", {"start": v(90.83, 5.04) * mm, "end": v(90.83, 8.4) * mm});
            skLineSegment(sketch, "E160", {"start": v(82.58, -0.8) * mm, "end": v(80.7, -0.8) * mm});
            skLineSegment(sketch, "E161", {"start": v(80.7, -0.8) * mm, "end": v(80.7, -4.46) * mm});
            skFitSpline(sketch, "E162", {"points": [v(88.9, 5.04) * mm, v(88.9, 5.96) * mm, v(88.81, 6.67) * mm, v(88.4, 7.26) * mm, v(87.7, 7.65) * mm, v(86.38, 7.74) * mm, v(85.55, 7.48) * mm, v(84.9, 6.92) * mm, v(84.54, 6.28) * mm, v(84.43, 5.54) * mm, v(84.62, 4.78) * mm, v(85.23, 4.24) * mm, v(86.52, 3.6) * mm, v(88.57, 2.81) * mm, v(90.1, 2) * mm, v(91.24, 1) * mm, v(91.8, 0.11) * mm, v(92, -0.84) * mm, v(91.92, -1.93) * mm, v(91.31, -3.24) * mm, v(90.25, -4.27) * mm, v(88.9, -5.04) * mm, v(87.46, -5.38) * mm, v(85.03, -5.43) * mm, v(82.73, -5.12) * mm, v(80.7, -4.46) * mm], "startDerivative": vector(0.22, 27.4) * mm, "endDerivative": vector(-38.02, 14.2) * mm});
            skFitSpline(sketch, "E163", {"points": [v(82.58, -0.8) * mm, v(82.69, -2.28) * mm, v(83.1, -3.16) * mm, v(83.96, -3.75) * mm, v(84.85, -4.05) * mm, v(85.98, -4.15) * mm, v(86.93, -3.96) * mm, v(87.6, -3.52) * mm, v(88.06, -2.86) * mm, v(88.14, -2.12) * mm, v(88.07, -1.47) * mm, v(87.4, -0.69) * mm, v(86.5, -0.12) * mm, v(84.59, 0.66) * mm, v(82.93, 1.48) * mm, v(82.03, 2.15) * mm, v(81.38, 2.83) * mm, v(80.8, 4.04) * mm, v(80.7, 5.31) * mm, v(81.1, 6.7) * mm, v(82.1, 7.82) * mm, v(83.5, 8.6) * mm, v(85.13, 9) * mm, v(86.58, 9.07) * mm, v(88.33, 8.95) * mm, v(89.8, 8.67) * mm, v(90.83, 8.4) * mm], "startDerivative": vector(0.74, -36.8) * mm, "endDerivative": vector(27.28, -7.87) * mm});
            skSolve(sketch);
        }
        {
            var Q0;
            Q0=makeQuery(id+"F0.imprint","IMPRINT",FACE,{"disambiguationData":[TD([[makeQuery(id+"F0.imprint","IMPRINT",EDGE,{"derivedFrom":sQuery(id+"F0.wireOp",EDGE,"E0")}),1.0]])]});
            var Q1;
            Q1=makeQuery(id+"F0.imprint","IMPRINT",FACE,{"disambiguationData":[TD([[makeQuery(id+"F0.imprint","IMPRINT",EDGE,{"derivedFrom":sQuery(id+"F0.wireOp",EDGE,"E13")}),-1.0]])]});
            var Q2;
            Q2=makeQuery(id+"F0.imprint","IMPRINT",FACE,{"disambiguationData":[TD([[makeQuery(id+"F0.imprint","IMPRINT",EDGE,{"derivedFrom":sQuery(id+"F0.wireOp",EDGE,"E29")}),-1.0]])]});
            var Q3;
            Q3=makeQuery(id+"F0.imprint","IMPRINT",FACE,{"disambiguationData":[TD([[makeQuery(id+"F0.imprint","IMPRINT",EDGE,{"derivedFrom":sQuery(id+"F0.wireOp",EDGE,"E28.bottom")}),-1.0]])]});
            var Q4;
            Q4=makeQuery(id+"F0.imprint","IMPRINT",FACE,{"disambiguationData":[TD([[makeQuery(id+"F0.imprint","IMPRINT",EDGE,{"derivedFrom":sQuery(id+"F0.wireOp",EDGE,"E39")}),-1.0]])]});
            var Q5;
            Q5=makeQuery(id+"F0.imprint","IMPRINT",FACE,{"disambiguationData":[TD([[makeQuery(id+"F0.imprint","IMPRINT",EDGE,{"derivedFrom":sQuery(id+"F0.wireOp",EDGE,"E59")}),-1.0]])]});
            var Q6;
            Q6=makeQuery(id+"F0.imprint","IMPRINT",FACE,{"disambiguationData":[TD([[makeQuery(id+"F0.imprint","IMPRINT",EDGE,{"derivedFrom":sQuery(id+"F0.wireOp",EDGE,"E74")}),-1.0]])]});
            var Q7;
            Q7=makeQuery(id+"F0.imprint","IMPRINT",FACE,{"disambiguationData":[TD([[makeQuery(id+"F0.imprint","IMPRINT",EDGE,{"derivedFrom":sQuery(id+"F0.wireOp",EDGE,"E73.bottom")}),1.0]])]});
            var Q8;
            Q8=makeQuery(id+"F0.imprint","IMPRINT",FACE,{"disambiguationData":[TD([[makeQuery(id+"F0.imprint","IMPRINT",EDGE,{"derivedFrom":sQuery(id+"F0.wireOp",EDGE,"E84")}),-1.0]])]});
            var Q9;
            Q9=makeQuery(id+"F0.imprint","IMPRINT",FACE,{"disambiguationData":[TD([[makeQuery(id+"F0.imprint","IMPRINT",EDGE,{"derivedFrom":sQuery(id+"F0.wireOp",EDGE,"E132")}),-1.0]])]});
            var Q10;
            Q10=makeQuery(id+"F0.imprint","IMPRINT",FACE,{"disambiguationData":[TD([[makeQuery(id+"F0.imprint","IMPRINT",EDGE,{"derivedFrom":sQuery(id+"F0.wireOp",EDGE,"E104")}),1.0]])]});
            var Q11;
            Q11=makeQuery(id+"F0.imprint","IMPRINT",FACE,{"disambiguationData":[TD([[makeQuery(id+"F0.imprint","IMPRINT",EDGE,{"derivedFrom":sQuery(id+"F0.wireOp",EDGE,"E117")}),-1.0]])]});
            var Q12;
            Q12=makeQuery(id+"F0.imprint","IMPRINT",FACE,{"disambiguationData":[TD([[makeQuery(id+"F0.imprint","IMPRINT",EDGE,{"derivedFrom":sQuery(id+"F0.wireOp",EDGE,"E142")}),1.0]])]});
            var Q13;
            Q13=makeQuery(id+"F0.imprint","IMPRINT",FACE,{"disambiguationData":[TD([[makeQuery(id+"F0.imprint","IMPRINT",EDGE,{"derivedFrom":sQuery(id+"F0.wireOp",EDGE,"E144")}),-1.0]])]});
            var Q14;
            Q14=makeQuery(id+"F0.imprint","IMPRINT",FACE,{"disambiguationData":[TD([[makeQuery(id+"F0.imprint","IMPRINT",EDGE,{"derivedFrom":sQuery(id+"F0.wireOp",EDGE,"E158")}),1.0]])]});
            extrude(context, id + "F1", {"entities" : qUnion([Q0, Q1, Q2, Q3, Q4, Q5, Q6, Q7, Q8, Q9, Q10, Q11, Q12, Q13, Q14]), "depth" : 12.7 * mm});
        }
        {
            var Q0;
            Q0=qCreatedBy(makeId("Front.planeOp"),FACE);
            var sketch = newSketch(context, id + "F2", { "sketchPlane" : qUnion([Q0])});
            skLineSegment(sketch, "E164.bottom", {"start": v(-95.68, 16.95) * mm, "end": v(95.29, 16.95) * mm});
            skLineSegment(sketch, "E164.top", {"start": v(-95.68, -13.3) * mm, "end": v(95.29, -13.3) * mm});
            skLineSegment(sketch, "E164.left", {"start": v(-95.68, 16.95) * mm, "end": v(-95.68, -13.3) * mm});
            skLineSegment(sketch, "E164.right", {"start": v(95.29, 16.95) * mm, "end": v(95.29, -13.3) * mm});
            skSolve(sketch);
        }
        {
            var Q0;
            Q0=makeQuery(id+"F2.imprint","IMPRINT",FACE,{"disambiguationData":[TD([[makeQuery(id+"F2.imprint","IMPRINT",EDGE,{"derivedFrom":sQuery(id+"F2.wireOp",EDGE,"E164.bottom")}),-1.0]])]});
            extrude(context, id + "F3", {"entities" : qUnion([Q0]), "depth" : 10.16 * mm});
        }
        {
            var Q0;
            Q0=makeQuery(id+"F3.opExtrude","CAP_FACE",FACE,{"disambiguationData":[OSD([sQuery(id+"F2.wireOp",EDGE,"E164.bottom"),sQuery(id+"F2.wireOp",EDGE,"E164.top"),sQuery(id+"F2.wireOp",EDGE,"E164.left"),sQuery(id+"F2.wireOp",EDGE,"E164.right")])],"isStart":false});
            var sketch = newSketch(context, id + "F4", { "sketchPlane" : qUnion([Q0])});
            skLineSegment(sketch, "E165.0", {"start": v(-93.14, 14.41) * mm, "end": v(-93.14, -10.77) * mm});
            skLineSegment(sketch, "E165.1", {"start": v(92.75, 14.41) * mm, "end": v(-93.14, 14.41) * mm});
            skLineSegment(sketch, "E165.2", {"start": v(92.75, -10.77) * mm, "end": v(92.75, 14.41) * mm});
            skLineSegment(sketch, "E165.3", {"start": v(-93.14, -10.77) * mm, "end": v(92.75, -10.77) * mm});
            skSolve(sketch);
        }
        {
            var Q0;
            Q0=makeQuery(id+"F4.imprint","IMPRINT",FACE,{"disambiguationData":[TD([[makeQuery(id+"F4.imprint","IMPRINT",EDGE,{"derivedFrom":sQuery(id+"F4.wireOp",EDGE,"E165.0")}),1.0]])]});
            extrude(context, id + "F5", {"entities" : qUnion([Q0]), "operationType" : NewBodyOperationType.REMOVE, "oppositeDirection" : true, "depth" : 3.8 * mm, "hasDraft" : true, "draftAngle" : 45 * degree, "draftPullDirection" : true});
        }
        {
            var Q0;
            Q0=makeQuery(id+"F1.opExtrude","CAP_FACE",FACE,{"disambiguationData":[OSD([sQuery(id+"F0.wireOp",EDGE,"E0"),sQuery(id+"F0.wireOp",EDGE,"E1"),sQuery(id+"F0.wireOp",EDGE,"E2"),sQuery(id+"F0.wireOp",EDGE,"E3"),sQuery(id+"F0.wireOp",EDGE,"E4"),sQuery(id+"F0.wireOp",EDGE,"E5"),sQuery(id+"F0.wireOp",EDGE,"E6"),sQuery(id+"F0.wireOp",EDGE,"E7"),sQuery(id+"F0.wireOp",EDGE,"E8"),sQuery(id+"F0.wireOp",EDGE,"E9"),sQuery(id+"F0.wireOp",EDGE,"E10"),sQuery(id+"F0.wireOp",EDGE,"E11"),sQuery(id+"F0.wireOp",EDGE,"E12")])],"isStart":false});
            var Q1;
            Q1=makeQuery(id+"F1.opExtrude","CAP_FACE",FACE,{"disambiguationData":[OSD([sQuery(id+"F0.wireOp",EDGE,"E13"),sQuery(id+"F0.wireOp",EDGE,"E14"),sQuery(id+"F0.wireOp",EDGE,"E15"),sQuery(id+"F0.wireOp",EDGE,"E16"),sQuery(id+"F0.wireOp",EDGE,"E17"),sQuery(id+"F0.wireOp",EDGE,"E18"),sQuery(id+"F0.wireOp",EDGE,"E19"),sQuery(id+"F0.wireOp",EDGE,"E20"),sQuery(id+"F0.wireOp",EDGE,"E21"),sQuery(id+"F0.wireOp",EDGE,"E22"),sQuery(id+"F0.wireOp",EDGE,"E23"),sQuery(id+"F0.wireOp",EDGE,"E24"),sQuery(id+"F0.wireOp",EDGE,"E25"),sQuery(id+"F0.wireOp",EDGE,"E26"),sQuery(id+"F0.wireOp",EDGE,"E27")])],"isStart":false});
            var Q2;
            Q2=makeQuery(id+"F1.opExtrude","CAP_FACE",FACE,{"disambiguationData":[OSD([sQuery(id+"F0.wireOp",EDGE,"E29"),sQuery(id+"F0.wireOp",EDGE,"E30"),sQuery(id+"F0.wireOp",EDGE,"E31"),sQuery(id+"F0.wireOp",EDGE,"E32"),sQuery(id+"F0.wireOp",EDGE,"E33"),sQuery(id+"F0.wireOp",EDGE,"E34"),sQuery(id+"F0.wireOp",EDGE,"E35"),sQuery(id+"F0.wireOp",EDGE,"E36"),sQuery(id+"F0.wireOp",EDGE,"E37"),sQuery(id+"F0.wireOp",EDGE,"E38")])],"isStart":false});
            var Q3;
            Q3=makeQuery(id+"F1.opExtrude","CAP_FACE",FACE,{"disambiguationData":[OSD([sQuery(id+"F0.wireOp",EDGE,"E28.bottom"),sQuery(id+"F0.wireOp",EDGE,"E28.top"),sQuery(id+"F0.wireOp",EDGE,"E28.left"),sQuery(id+"F0.wireOp",EDGE,"E28.right")])],"isStart":false});
            var Q4;
            Q4=makeQuery(id+"F1.opExtrude","CAP_FACE",FACE,{"disambiguationData":[OSD([sQuery(id+"F0.wireOp",EDGE,"E39"),sQuery(id+"F0.wireOp",EDGE,"E40"),sQuery(id+"F0.wireOp",EDGE,"E41"),sQuery(id+"F0.wireOp",EDGE,"E42"),sQuery(id+"F0.wireOp",EDGE,"E43"),sQuery(id+"F0.wireOp",EDGE,"E44"),sQuery(id+"F0.wireOp",EDGE,"E45"),sQuery(id+"F0.wireOp",EDGE,"E46"),sQuery(id+"F0.wireOp",EDGE,"E47"),sQuery(id+"F0.wireOp",EDGE,"E48"),sQuery(id+"F0.wireOp",EDGE,"E49"),sQuery(id+"F0.wireOp",EDGE,"E50"),sQuery(id+"F0.wireOp",EDGE,"E51"),sQuery(id+"F0.wireOp",EDGE,"E52"),sQuery(id+"F0.wireOp",EDGE,"E53"),sQuery(id+"F0.wireOp",EDGE,"E54"),sQuery(id+"F0.wireOp",EDGE,"E55"),sQuery(id+"F0.wireOp",EDGE,"E56"),sQuery(id+"F0.wireOp",EDGE,"E57"),sQuery(id+"F0.wireOp",EDGE,"E58")])],"isStart":false});
            var Q5;
            Q5=makeQuery(id+"F1.opExtrude","CAP_FACE",FACE,{"disambiguationData":[OSD([sQuery(id+"F0.wireOp",EDGE,"E59"),sQuery(id+"F0.wireOp",EDGE,"E60"),sQuery(id+"F0.wireOp",EDGE,"E61"),sQuery(id+"F0.wireOp",EDGE,"E62"),sQuery(id+"F0.wireOp",EDGE,"E63"),sQuery(id+"F0.wireOp",EDGE,"E64"),sQuery(id+"F0.wireOp",EDGE,"E65"),sQuery(id+"F0.wireOp",EDGE,"E66"),sQuery(id+"F0.wireOp",EDGE,"E67"),sQuery(id+"F0.wireOp",EDGE,"E68"),sQuery(id+"F0.wireOp",EDGE,"E69"),sQuery(id+"F0.wireOp",EDGE,"E70"),sQuery(id+"F0.wireOp",EDGE,"E71"),sQuery(id+"F0.wireOp",EDGE,"E72")])],"isStart":false});
            var Q6;
            Q6=makeQuery(id+"F1.opExtrude","CAP_FACE",FACE,{"disambiguationData":[OSD([sQuery(id+"F0.wireOp",EDGE,"E74"),sQuery(id+"F0.wireOp",EDGE,"E75"),sQuery(id+"F0.wireOp",EDGE,"E76"),sQuery(id+"F0.wireOp",EDGE,"E77"),sQuery(id+"F0.wireOp",EDGE,"E78"),sQuery(id+"F0.wireOp",EDGE,"E79"),sQuery(id+"F0.wireOp",EDGE,"E80"),sQuery(id+"F0.wireOp",EDGE,"E81"),sQuery(id+"F0.wireOp",EDGE,"E82"),sQuery(id+"F0.wireOp",EDGE,"E83")])],"isStart":false});
            var Q7;
            Q7=makeQuery(id+"F1.opExtrude","CAP_FACE",FACE,{"disambiguationData":[OSD([sQuery(id+"F0.wireOp",EDGE,"E73.bottom"),sQuery(id+"F0.wireOp",EDGE,"E73.top"),sQuery(id+"F0.wireOp",EDGE,"E73.left"),sQuery(id+"F0.wireOp",EDGE,"E73.right")])],"isStart":false});
            var Q8;
            Q8=makeQuery(id+"F1.opExtrude","CAP_FACE",FACE,{"disambiguationData":[OSD([sQuery(id+"F0.wireOp",EDGE,"E84"),sQuery(id+"F0.wireOp",EDGE,"E85"),sQuery(id+"F0.wireOp",EDGE,"E86"),sQuery(id+"F0.wireOp",EDGE,"E87"),sQuery(id+"F0.wireOp",EDGE,"E88"),sQuery(id+"F0.wireOp",EDGE,"E89"),sQuery(id+"F0.wireOp",EDGE,"E90"),sQuery(id+"F0.wireOp",EDGE,"E91"),sQuery(id+"F0.wireOp",EDGE,"E92"),sQuery(id+"F0.wireOp",EDGE,"E93"),sQuery(id+"F0.wireOp",EDGE,"E94"),sQuery(id+"F0.wireOp",EDGE,"E95"),sQuery(id+"F0.wireOp",EDGE,"E96"),sQuery(id+"F0.wireOp",EDGE,"E97"),sQuery(id+"F0.wireOp",EDGE,"E98"),sQuery(id+"F0.wireOp",EDGE,"E99"),sQuery(id+"F0.wireOp",EDGE,"E100"),sQuery(id+"F0.wireOp",EDGE,"E101"),sQuery(id+"F0.wireOp",EDGE,"E102"),sQuery(id+"F0.wireOp",EDGE,"E103")])],"isStart":false});
            var Q9;
            Q9=makeQuery(id+"F1.opExtrude","CAP_FACE",FACE,{"disambiguationData":[OSD([sQuery(id+"F0.wireOp",EDGE,"E132"),sQuery(id+"F0.wireOp",EDGE,"E133"),sQuery(id+"F0.wireOp",EDGE,"E134"),sQuery(id+"F0.wireOp",EDGE,"E135"),sQuery(id+"F0.wireOp",EDGE,"E136"),sQuery(id+"F0.wireOp",EDGE,"E137"),sQuery(id+"F0.wireOp",EDGE,"E138"),sQuery(id+"F0.wireOp",EDGE,"E139"),sQuery(id+"F0.wireOp",EDGE,"E140"),sQuery(id+"F0.wireOp",EDGE,"E141")])],"isStart":false});
            var Q10;
            Q10=makeQuery(id+"F1.opExtrude","CAP_FACE",FACE,{"disambiguationData":[OSD([sQuery(id+"F0.wireOp",EDGE,"E104"),sQuery(id+"F0.wireOp",EDGE,"E105"),sQuery(id+"F0.wireOp",EDGE,"E106"),sQuery(id+"F0.wireOp",EDGE,"E107"),sQuery(id+"F0.wireOp",EDGE,"E108"),sQuery(id+"F0.wireOp",EDGE,"E109"),sQuery(id+"F0.wireOp",EDGE,"E110"),sQuery(id+"F0.wireOp",EDGE,"E111"),sQuery(id+"F0.wireOp",EDGE,"E112"),sQuery(id+"F0.wireOp",EDGE,"E113"),sQuery(id+"F0.wireOp",EDGE,"E114"),sQuery(id+"F0.wireOp",EDGE,"E115"),sQuery(id+"F0.wireOp",EDGE,"E116")])],"isStart":false});
            var Q11;
            Q11=makeQuery(id+"F1.opExtrude","CAP_FACE",FACE,{"disambiguationData":[OSD([sQuery(id+"F0.wireOp",EDGE,"E117"),sQuery(id+"F0.wireOp",EDGE,"E118"),sQuery(id+"F0.wireOp",EDGE,"E119"),sQuery(id+"F0.wireOp",EDGE,"E120"),sQuery(id+"F0.wireOp",EDGE,"E121"),sQuery(id+"F0.wireOp",EDGE,"E122"),sQuery(id+"F0.wireOp",EDGE,"E123"),sQuery(id+"F0.wireOp",EDGE,"E124"),sQuery(id+"F0.wireOp",EDGE,"E125"),sQuery(id+"F0.wireOp",EDGE,"E126"),sQuery(id+"F0.wireOp",EDGE,"E127"),sQuery(id+"F0.wireOp",EDGE,"E128"),sQuery(id+"F0.wireOp",EDGE,"E129"),sQuery(id+"F0.wireOp",EDGE,"E130"),sQuery(id+"F0.wireOp",EDGE,"E131")])],"isStart":false});
            var Q12;
            Q12=makeQuery(id+"F1.opExtrude","CAP_FACE",FACE,{"disambiguationData":[OSD([sQuery(id+"F0.wireOp",EDGE,"E142"),sQuery(id+"F0.wireOp",EDGE,"E143")])],"isStart":false});
            var Q13;
            Q13=makeQuery(id+"F1.opExtrude","CAP_FACE",FACE,{"disambiguationData":[OSD([sQuery(id+"F0.wireOp",EDGE,"E158"),sQuery(id+"F0.wireOp",EDGE,"E159"),sQuery(id+"F0.wireOp",EDGE,"E160"),sQuery(id+"F0.wireOp",EDGE,"E161"),sQuery(id+"F0.wireOp",EDGE,"E162"),sQuery(id+"F0.wireOp",EDGE,"E163")])],"isStart":false});
            var Q14;
            Q14=makeQuery(id+"F1.opExtrude","CAP_FACE",FACE,{"disambiguationData":[OSD([sQuery(id+"F0.wireOp",EDGE,"E144"),sQuery(id+"F0.wireOp",EDGE,"E145"),sQuery(id+"F0.wireOp",EDGE,"E146"),sQuery(id+"F0.wireOp",EDGE,"E147"),sQuery(id+"F0.wireOp",EDGE,"E148"),sQuery(id+"F0.wireOp",EDGE,"E149"),sQuery(id+"F0.wireOp",EDGE,"E150"),sQuery(id+"F0.wireOp",EDGE,"E151"),sQuery(id+"F0.wireOp",EDGE,"E152"),sQuery(id+"F0.wireOp",EDGE,"E153"),sQuery(id+"F0.wireOp",EDGE,"E154"),sQuery(id+"F0.wireOp",EDGE,"E155"),sQuery(id+"F0.wireOp",EDGE,"E156"),sQuery(id+"F0.wireOp",EDGE,"E157")])],"isStart":false});
            fillet(context, id + "F6", {"entities" : qUnion([Q0, Q1, Q2, Q3, Q4, Q5, Q6, Q7, Q8, Q9, Q10, Q11, Q12, Q13, Q14]), "radius" : 0.5 * mm, "tangentPropagation" : true, "allowEdgeOverflow" : false});
        }
        {
            var Q0;
            Q0=makeQuery(id+"F2.imprint","IMPRINT",FACE,{"disambiguationData":[TD([[makeQuery(id+"F2.imprint","IMPRINT",EDGE,{"derivedFrom":sQuery(id+"F2.wireOp",EDGE,"E164.bottom")}),-1.0]])]});
            extrude(context, id + "F7", {"entities" : qUnion([Q0]), "operationType" : NewBodyOperationType.REMOVE, "depth" : 4.34 * mm});
        }
        {
            var Q0;
            Q0=makeQuery(id+"F3.opExtrude","SWEPT_EDGE",EDGE,{"disambiguationData":[OSD([sQuery(id+"F2.wireOp",EDGE,"E164.top"),sQuery(id+"F2.wireOp",EDGE,"E164.left")])]});
            var Q1;
            Q1=makeQuery(id+"F3.opExtrude","CAP_EDGE",EDGE,{"disambiguationData":[OSD([sQuery(id+"F2.wireOp",EDGE,"E164.top")])],"isStart":false});
            var Q2;
            Q2=makeQuery(id+"F3.opExtrude","CAP_EDGE",EDGE,{"disambiguationData":[OSD([sQuery(id+"F2.wireOp",EDGE,"E164.left")])],"isStart":false});
            var Q3;
            Q3=makeQuery(id+"F3.opExtrude","SWEPT_EDGE",EDGE,{"disambiguationData":[OSD([sQuery(id+"F2.wireOp",EDGE,"E164.bottom"),sQuery(id+"F2.wireOp",EDGE,"E164.left")])]});
            var Q4;
            Q4=makeQuery(id+"F3.opExtrude","CAP_EDGE",EDGE,{"disambiguationData":[OSD([sQuery(id+"F2.wireOp",EDGE,"E164.bottom")])],"isStart":false});
            var Q5;
            Q5=makeQuery(id+"F3.opExtrude","SWEPT_EDGE",EDGE,{"disambiguationData":[OSD([sQuery(id+"F2.wireOp",EDGE,"E164.top"),sQuery(id+"F2.wireOp",EDGE,"E164.right")])]});
            var Q6;
            Q6=makeQuery(id+"F3.opExtrude","CAP_EDGE",EDGE,{"disambiguationData":[OSD([sQuery(id+"F2.wireOp",EDGE,"E164.right")])],"isStart":false});
            var Q7;
            Q7=makeQuery(id+"F3.opExtrude","SWEPT_EDGE",EDGE,{"disambiguationData":[OSD([sQuery(id+"F2.wireOp",EDGE,"E164.bottom"),sQuery(id+"F2.wireOp",EDGE,"E164.right")])]});
            var Q8;
            Q8=makeQuery(id+"F7.boolean.opBoolean","COPY",EDGE,{"derivedFrom":makeQuery(id+"F7.opExtrude","CAP_EDGE",EDGE,{"disambiguationData":[OSD([sQuery(id+"F2.wireOp",EDGE,"E164.top")])],"isStart":false})});
            var Q9;
            Q9=makeQuery(id+"F7.boolean.opBoolean","COPY",EDGE,{"derivedFrom":makeQuery(id+"F7.opExtrude","CAP_EDGE",EDGE,{"disambiguationData":[OSD([sQuery(id+"F2.wireOp",EDGE,"E164.left")])],"isStart":false})});
            var Q10;
            Q10=makeQuery(id+"F7.boolean.opBoolean","COPY",EDGE,{"derivedFrom":makeQuery(id+"F7.opExtrude","CAP_EDGE",EDGE,{"disambiguationData":[OSD([sQuery(id+"F2.wireOp",EDGE,"E164.bottom")])],"isStart":false})});
            var Q11;
            Q11=makeQuery(id+"F7.boolean.opBoolean","COPY",EDGE,{"derivedFrom":makeQuery(id+"F7.opExtrude","CAP_EDGE",EDGE,{"disambiguationData":[OSD([sQuery(id+"F2.wireOp",EDGE,"E164.right")])],"isStart":false})});
            chamfer(context, id + "F8", {"entities" : qUnion([Q0, Q1, Q2, Q3, Q4, Q5, Q6, Q7, Q8, Q9, Q10, Q11]), "width" : 2.54 * mm, "tangentPropagation" : true});
        }
    });
